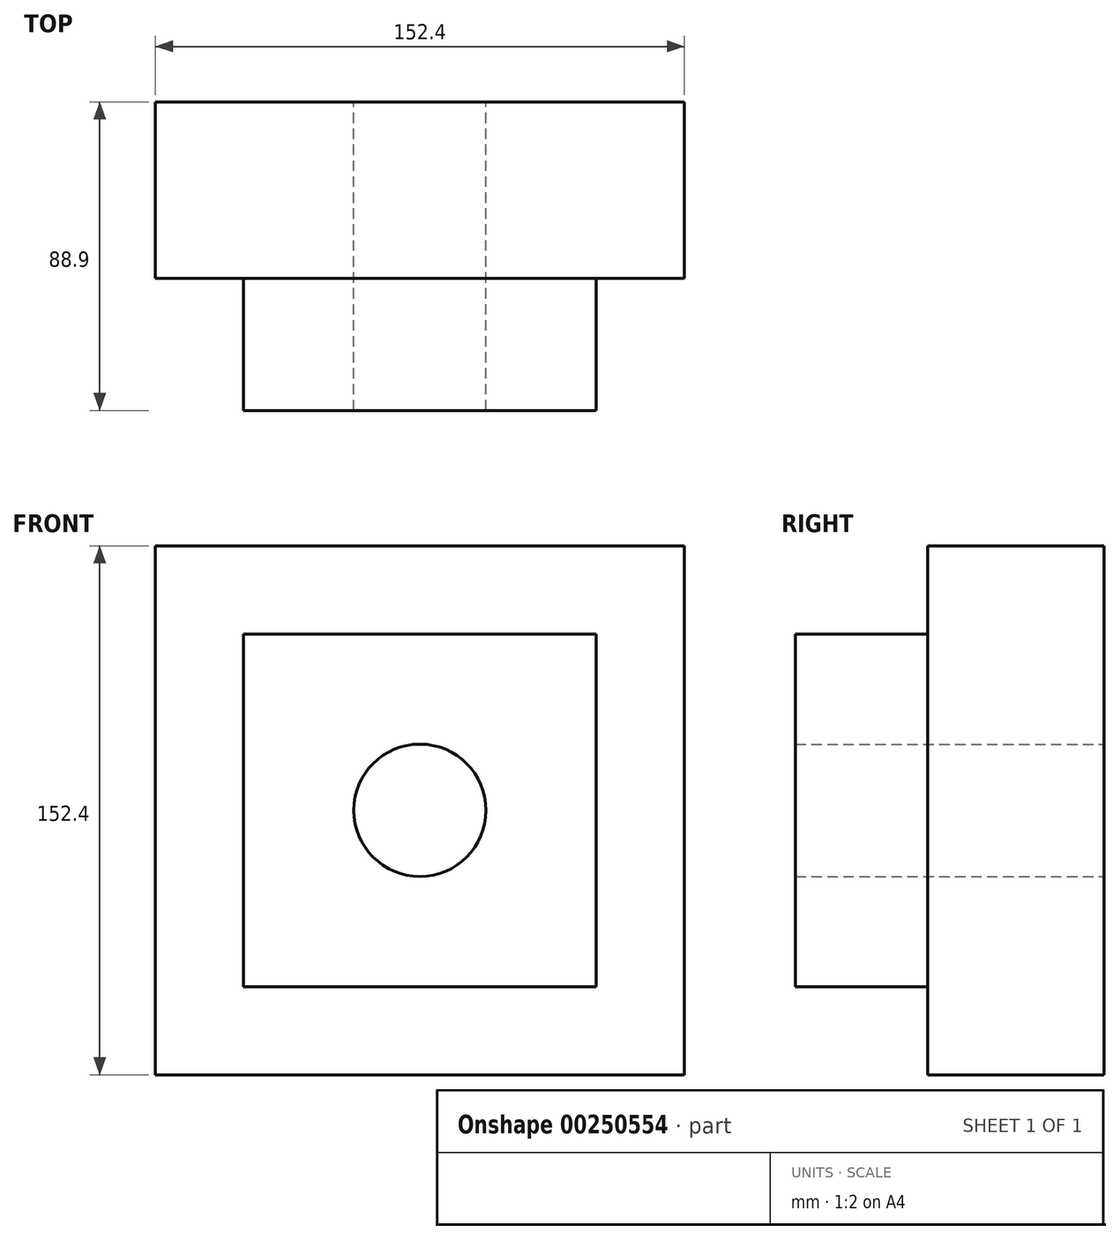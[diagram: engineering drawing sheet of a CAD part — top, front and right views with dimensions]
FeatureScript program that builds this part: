
annotation { "Feature Type Name" : "Feature", "Feature Type Description" : "" }
export const myFeature = defineFeature(function(context is Context, id is Id, definition is map)
    precondition{}
    {
        {
            var Q0;
            Q0=qCreatedBy(makeId("Front.planeOp"),FACE);
            var sketch = newSketch(context, id + "F0", { "sketchPlane" : qUnion([Q0])});
            skCircle(sketch, "E0", {"center": v(0, 0) * mm, "radius": 19.05 * mm});
            skLineSegment(sketch, "E1.bottom", {"start": v(50.8, 50.8) * mm, "end": v(-50.8, 50.8) * mm});
            skLineSegment(sketch, "E1.top", {"start": v(50.8, -50.8) * mm, "end": v(-50.8, -50.8) * mm});
            skLineSegment(sketch, "E1.left", {"start": v(50.8, 50.8) * mm, "end": v(50.8, -50.8) * mm});
            skLineSegment(sketch, "E1.right", {"start": v(-50.8, 50.8) * mm, "end": v(-50.8, -50.8) * mm});
            skLineSegment(sketch, "E2.bottom", {"start": v(76.2, 76.2) * mm, "end": v(-76.2, 76.2) * mm});
            skLineSegment(sketch, "E2.top", {"start": v(76.2, -76.2) * mm, "end": v(-76.2, -76.2) * mm});
            skLineSegment(sketch, "E2.left", {"start": v(76.2, 76.2) * mm, "end": v(76.2, -76.2) * mm});
            skLineSegment(sketch, "E2.right", {"start": v(-76.2, 76.2) * mm, "end": v(-76.2, -76.2) * mm});
            skSolve(sketch);
        }
        {
            var Q0;
            Q0=makeQuery(id+"F0.imprint","IMPRINT",FACE,{"disambiguationData":[TD([[makeQuery(id+"F0.imprint","IMPRINT",EDGE,{"derivedFrom":sQuery(id+"F0.wireOp",EDGE,"E0")}),-1.0]])]});
            extrude(context, id + "F1", {"entities" : qUnion([Q0]), "depth" : 38.1 * mm});
        }
        {
            var Q0;
            Q0 = qSketchRegion(id + "F0", true);
            var Q1;
            Q1=makeQuery(id+"F0.imprint","IMPRINT",FACE,{"disambiguationData":[TD([[makeQuery(id+"F0.imprint","IMPRINT",EDGE,{"derivedFrom":sQuery(id+"F0.wireOp",EDGE,"E0")}),-1.0]])]});
            var Q2;
            Q2=makeQuery(id+"F1.opExtrude","CAP_FACE",FACE,{"disambiguationData":[OSD([sQuery(id+"F0.wireOp",EDGE,"E0"),sQuery(id+"F0.wireOp",EDGE,"E1.bottom"),sQuery(id+"F0.wireOp",EDGE,"E1.top"),sQuery(id+"F0.wireOp",EDGE,"E1.left"),sQuery(id+"F0.wireOp",EDGE,"E1.right")])],"isStart":false});
            extrude(context, id + "F2", {"entities" : qUnion([Q0, Q1, Q2]), "operationType" : NewBodyOperationType.ADD, "depth" : 50.8 * mm});
        }
    });
